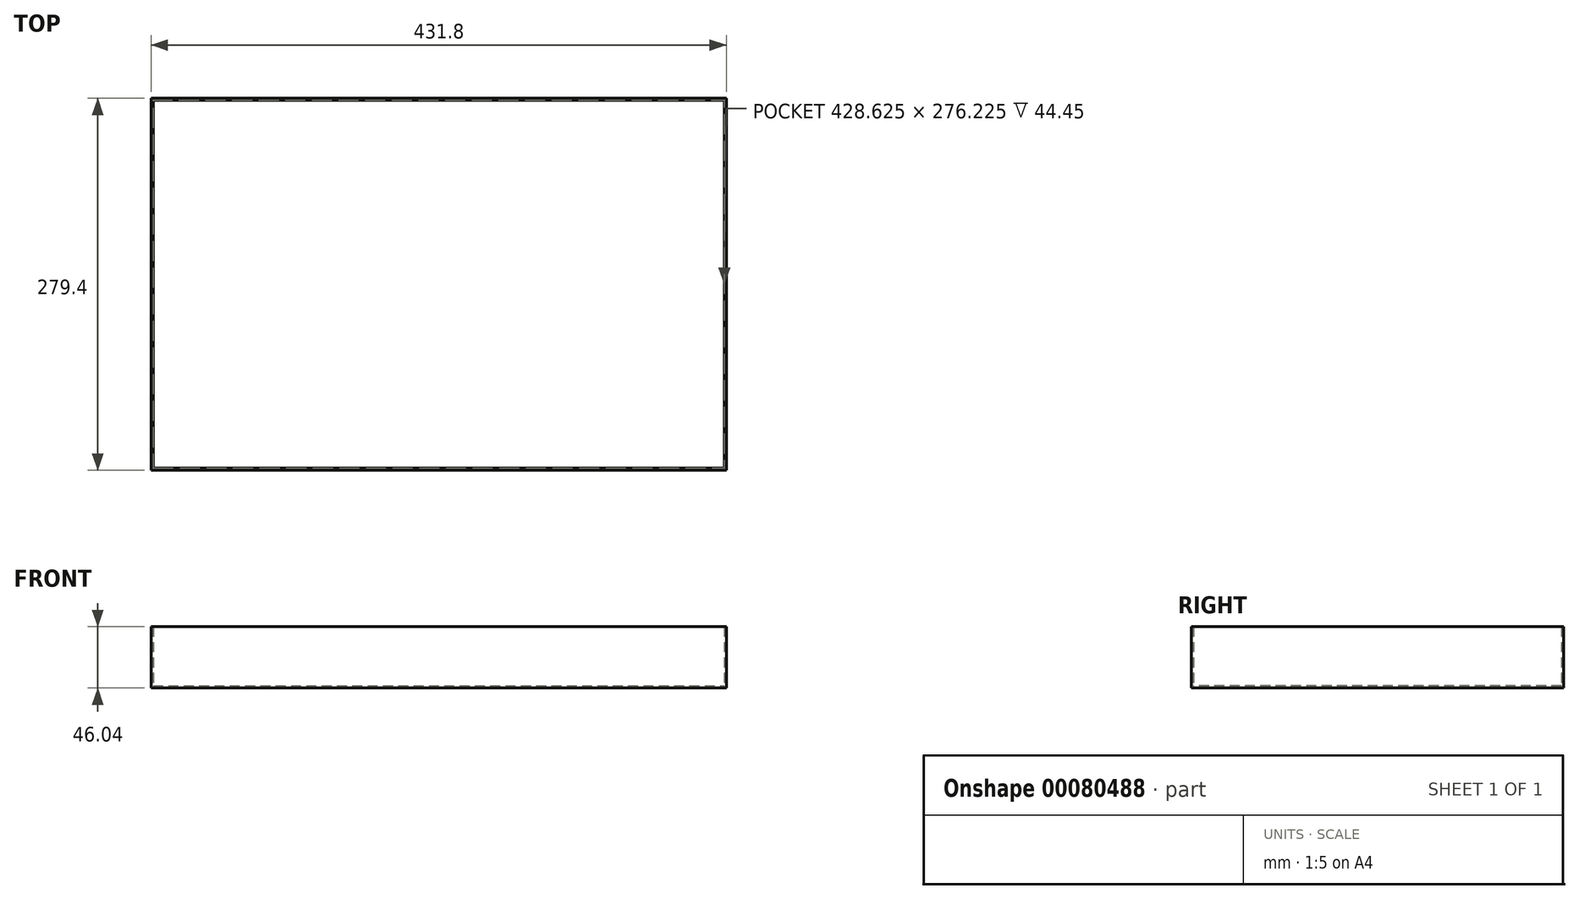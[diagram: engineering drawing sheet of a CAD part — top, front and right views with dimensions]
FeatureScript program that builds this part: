
annotation { "Feature Type Name" : "Feature", "Feature Type Description" : "" }
export const myFeature = defineFeature(function(context is Context, id is Id, definition is map)
    precondition{}
    {
        {
            var Q0;
            Q0=qCreatedBy(makeId("Top.planeOp"),FACE);
            var sketch = newSketch(context, id + "F0", { "sketchPlane" : qUnion([Q0])});
            skLineSegment(sketch, "E0.bottom", {"start": v(215.9, -139.7) * mm, "end": v(-215.9, -139.7) * mm});
            skLineSegment(sketch, "E0.top", {"start": v(215.9, 139.7) * mm, "end": v(-215.9, 139.7) * mm});
            skLineSegment(sketch, "E0.left", {"start": v(215.9, -139.7) * mm, "end": v(215.9, 139.7) * mm});
            skLineSegment(sketch, "E0.right", {"start": v(-215.9, -139.7) * mm, "end": v(-215.9, 139.7) * mm});
            skPoint(sketch, "E0.middle", {"position": v(0, 0) * mm});
            skSolve(sketch);
        }
        {
            var Q0;
            Q0=makeQuery(id+"F0.imprint","IMPRINT",FACE,{"disambiguationData":[TD([[makeQuery(id+"F0.imprint","IMPRINT",EDGE,{"derivedFrom":sQuery(id+"F0.wireOp",EDGE,"E0.bottom")}),-1.0]])]});
            extrude(context, id + "F1", {"entities" : qUnion([Q0]), "depth" : 1.59 * mm});
        }
        {
            var Q0;
            Q0=makeQuery(id+"F1.opExtrude","CAP_FACE",FACE,{"disambiguationData":[OSD([sQuery(id+"F0.wireOp",EDGE,"E0.bottom"),sQuery(id+"F0.wireOp",EDGE,"E0.top"),sQuery(id+"F0.wireOp",EDGE,"E0.left"),sQuery(id+"F0.wireOp",EDGE,"E0.right")])],"isStart":false});
            var sketch = newSketch(context, id + "F2", { "sketchPlane" : qUnion([Q0])});
            skLineSegment(sketch, "E1.0", {"start": v(-214.31, -138.11) * mm, "end": v(214.31, -138.11) * mm});
            skLineSegment(sketch, "E1.1", {"start": v(-214.31, 138.11) * mm, "end": v(-214.31, -138.11) * mm});
            skLineSegment(sketch, "E1.2", {"start": v(214.31, 138.11) * mm, "end": v(-214.31, 138.11) * mm});
            skLineSegment(sketch, "E1.3", {"start": v(214.31, -138.11) * mm, "end": v(214.31, 138.11) * mm});
            skSolve(sketch);
        }
        {
            var Q0;
            Q0=makeQuery(id+"F2.imprint","IMPRINT",FACE,{"disambiguationData":[TD([[makeQuery(id+"F2.imprint","IMPRINT",EDGE,{"derivedFrom":sQuery(id+"F2.wireOp",EDGE,"E1.0")}),-1.0]])]});
            extrude(context, id + "F3", {"entities" : qUnion([Q0]), "operationType" : NewBodyOperationType.ADD, "depth" : 44.45 * mm});
        }
    });
